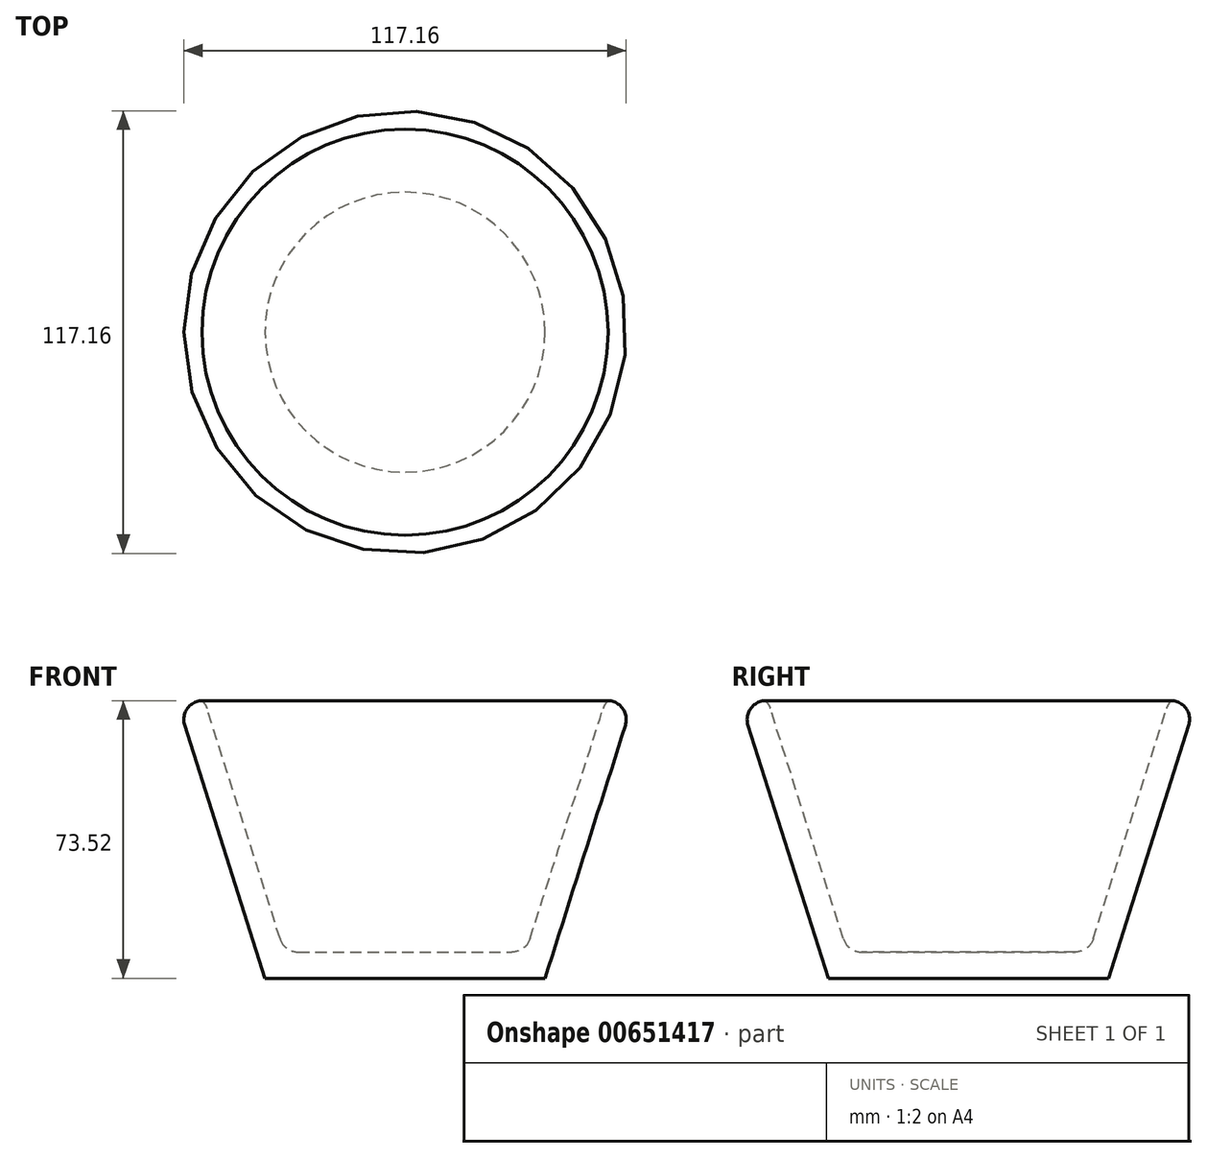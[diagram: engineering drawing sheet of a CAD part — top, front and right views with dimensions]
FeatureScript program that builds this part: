
annotation { "Feature Type Name" : "Feature", "Feature Type Description" : "" }
export const myFeature = defineFeature(function(context is Context, id is Id, definition is map)
    precondition{}
    {
        {
            var Q0;
            Q0=qCreatedBy(makeId("Front.planeOp"),FACE);
            var sketch = newSketch(context, id + "F0", { "sketchPlane" : qUnion([Q0])});
            skLineSegment(sketch, "E0", {"start": v(-60.34, 43.22) * mm, "end": v(-37.08, -30.06) * mm});
            skLineSegment(sketch, "E1", {"start": v(-37.08, -30.06) * mm, "end": v(0, -30.06) * mm});
            skLineSegment(sketch, "E2.0", {"start": v(-31.99, -23.1) * mm, "end": v(0, -23.1) * mm});
            skLineSegment(sketch, "E2.1", {"start": v(-53.12, 43.48) * mm, "end": v(-31.99, -23.1) * mm});
            skLineSegment(sketch, "E3", {"start": v(-60.34, 43.22) * mm, "end": v(-53.12, 43.48) * mm});
            skLineSegment(sketch, "E4", {"start": v(0, -23.1) * mm, "end": v(0, -30.06) * mm});
            skLineSegment(sketch, "E5", {"start": v(0, 52.55) * mm, "end": v(0, -47.17) * mm});
            skSolve(sketch);
        }
        {
            var Q0;
            Q0=makeQuery(id+"F0.imprint","IMPRINT",FACE,{"disambiguationData":[TD([[makeQuery(id+"F0.imprint","IMPRINT",EDGE,{"derivedFrom":sQuery(id+"F0.wireOp",EDGE,"E0")}),1.0]])]});
            var Q1;
            Q1=sQuery(id+"F0.wireOp",EDGE,"E5");
            revolve(context, id + "F1", {"entities" : qUnion([Q0]), "axis" : qUnion([Q1]), "revolveType" : RevolveType.FULL});
        }
        {
            var Q0;
            Q0=makeQuery(id+"F1.opRevolve","SWEPT_EDGE",EDGE,{"disambiguationData":[OSD([sQuery(id+"F0.wireOp",EDGE,"E0"),sQuery(id+"F0.wireOp",EDGE,"E3")])]});
            fillet(context, id + "F2", {"entities" : qUnion([Q0]), "radius" : 5 * mm, "tangentPropagation" : true, "allowEdgeOverflow" : false});
        }
        {
            var Q0;
            Q0=makeQuery(id+"F1.opRevolve","SWEPT_FACE",FACE,{"disambiguationData":[OSD([sQuery(id+"F0.wireOp",EDGE,"E2.1")])]});
            fillet(context, id + "F3", {"entities" : qUnion([Q0]), "radius" : 5 * mm, "tangentPropagation" : true, "allowEdgeOverflow" : false});
        }
    });
